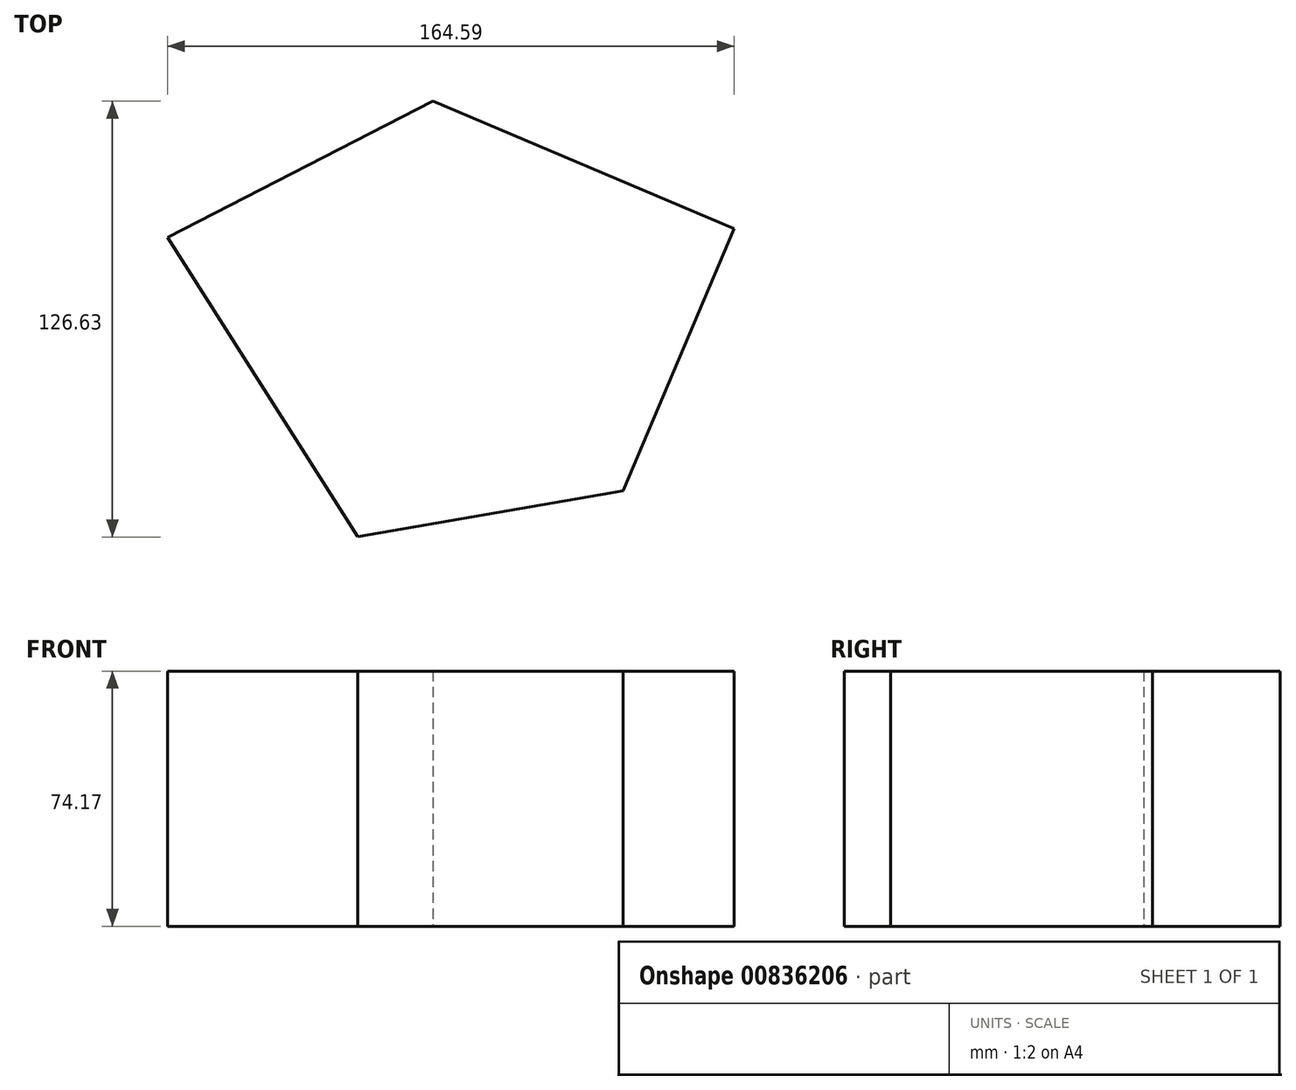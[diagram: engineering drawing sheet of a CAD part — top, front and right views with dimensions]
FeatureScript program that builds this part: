
annotation { "Feature Type Name" : "Feature", "Feature Type Description" : "" }
export const myFeature = defineFeature(function(context is Context, id is Id, definition is map)
    precondition{}
    {
        {
            var Q0;
            Q0=qCreatedBy(makeId("Top.planeOp"),FACE);
            var sketch = newSketch(context, id + "F0", { "sketchPlane" : qUnion([Q0])});
            skLineSegment(sketch, "E0", {"start": v(-60.78, -60.7) * mm, "end": v(-116, 26.37) * mm});
            skLineSegment(sketch, "E1", {"start": v(-116, 26.37) * mm, "end": v(-38.9, 65.93) * mm});
            skLineSegment(sketch, "E2", {"start": v(-38.9, 65.93) * mm, "end": v(48.59, 28.88) * mm});
            skLineSegment(sketch, "E3", {"start": v(48.59, 28.88) * mm, "end": v(16.33, -47.27) * mm});
            skLineSegment(sketch, "E4", {"start": v(16.33, -47.27) * mm, "end": v(-60.78, -60.7) * mm});
            skSolve(sketch);
        }
        {
            var Q0;
            Q0=makeQuery(id+"F0.imprint","IMPRINT",FACE,{"disambiguationData":[TD([[makeQuery(id+"F0.imprint","IMPRINT",EDGE,{"derivedFrom":sQuery(id+"F0.wireOp",EDGE,"E0")}),-1.0]])]});
            extrude(context, id + "F1", {"entities" : qUnion([Q0]), "depth" : 74.17 * mm, "offsetDistance" : 25.4 * mm});
        }
    });
